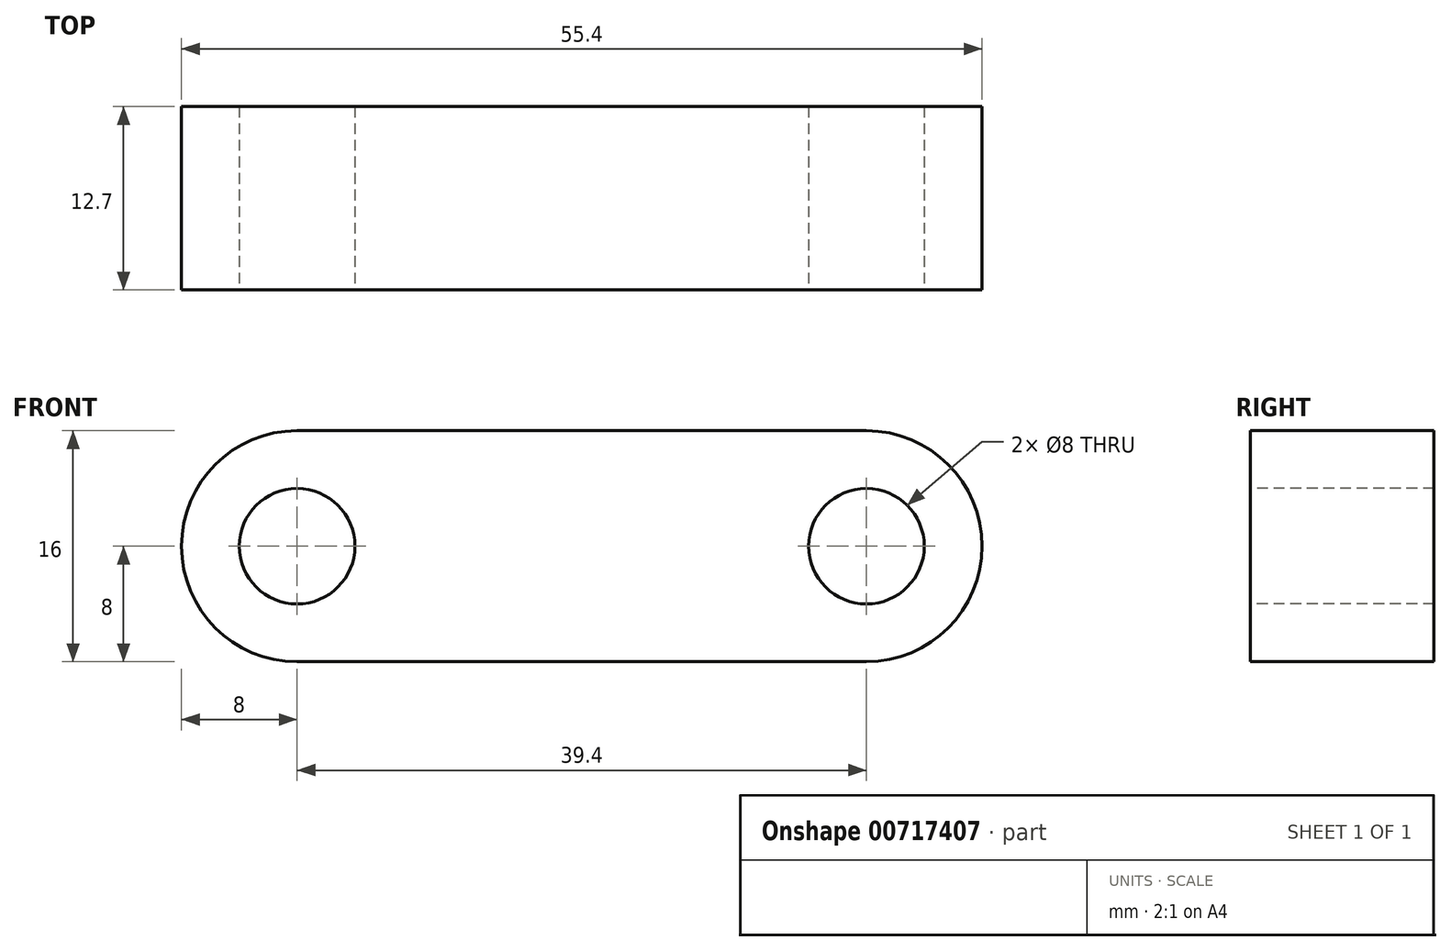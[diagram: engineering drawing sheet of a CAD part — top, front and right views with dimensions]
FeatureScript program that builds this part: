
annotation { "Feature Type Name" : "Feature", "Feature Type Description" : "" }
export const myFeature = defineFeature(function(context is Context, id is Id, definition is map)
    precondition{}
    {
        {
            var Q0;
            Q0=qCreatedBy(makeId("Front.planeOp"),FACE);
            var sketch = newSketch(context, id + "F0", { "sketchPlane" : qUnion([Q0])});
            skCircle(sketch, "E0", {"center": v(-39.4, 0) * mm, "radius": 8 * mm});
            skCircle(sketch, "E1", {"center": v(0, 0) * mm, "radius": 8 * mm});
            skLineSegment(sketch, "E2", {"start": v(-39.4, 8) * mm, "end": v(0, 8) * mm});
            skLineSegment(sketch, "E3", {"start": v(-39.4, -8) * mm, "end": v(0, -8) * mm});
            skSolve(sketch);
        }
        {
            var Q0;
            Q0 = qSketchRegion(id + "F0", true);
            extrude(context, id + "F1", {"entities" : qUnion([Q0]), "depth" : 12.7 * mm, "offsetDistance" : 25.4 * mm});
        }
        {
            var Q0;
            Q0=makeQuery(id+"F1.opExtrude","CAP_FACE",FACE,{"disambiguationData":[OSD([sQuery(id+"F0.wireOp",EDGE,"E0"),sQuery(id+"F0.wireOp",EDGE,"E1"),sQuery(id+"F0.wireOp",EDGE,"E2"),sQuery(id+"F0.wireOp",EDGE,"E3")])],"isStart":false});
            var sketch = newSketch(context, id + "F2", { "sketchPlane" : qUnion([Q0])});
            skCircle(sketch, "E4", {"center": v(-39.4, 0) * mm, "radius": 4 * mm});
            skCircle(sketch, "E5", {"center": v(0, 0) * mm, "radius": 4 * mm});
            skSolve(sketch);
        }
        {
            var Q0;
            Q0=makeQuery(id+"F2.imprint","IMPRINT",FACE,{"disambiguationData":[TD([[makeQuery(id+"F2.imprint","IMPRINT",EDGE,{"derivedFrom":sQuery(id+"F2.wireOp",EDGE,"E4")}),1.0]])]});
            var Q1;
            Q1=makeQuery(id+"F2.imprint","IMPRINT",FACE,{"disambiguationData":[TD([[makeQuery(id+"F2.imprint","IMPRINT",EDGE,{"derivedFrom":sQuery(id+"F2.wireOp",EDGE,"E5")}),1.0]])]});
            extrude(context, id + "F3", {"entities" : qUnion([Q0, Q1]), "operationType" : NewBodyOperationType.REMOVE, "endBound" : BoundingType.UP_TO_NEXT, "oppositeDirection" : true, "depth" : 25.4 * mm, "offsetDistance" : 25.4 * mm});
        }
    });
